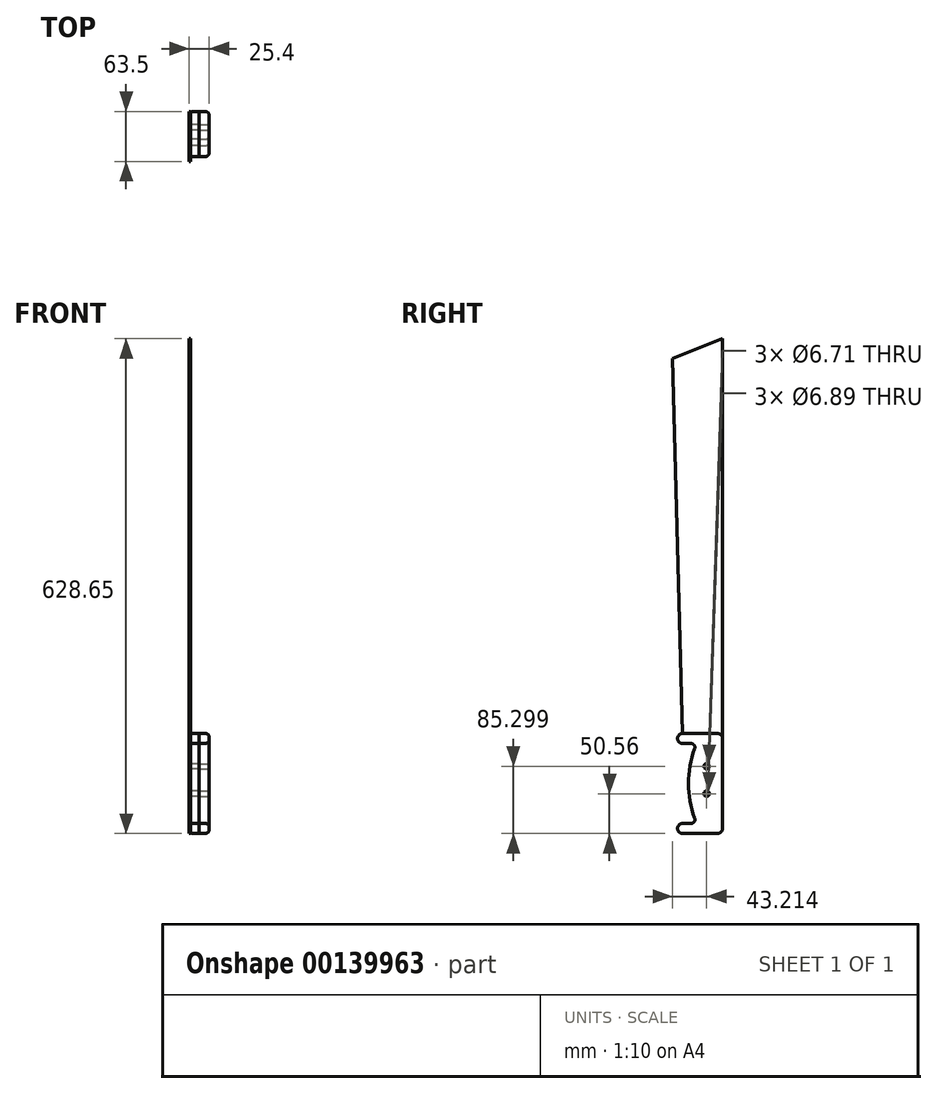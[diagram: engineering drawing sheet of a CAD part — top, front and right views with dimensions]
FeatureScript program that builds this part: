
annotation { "Feature Type Name" : "Feature", "Feature Type Description" : "" }
export const myFeature = defineFeature(function(context is Context, id is Id, definition is map)
    precondition{}
    {
        {
            var Q0;
            Q0=qCreatedBy(makeId("Right.planeOp"),FACE);
            var sketch = newSketch(context, id + "F0", { "sketchPlane" : qUnion([Q0])});
            skLineSegment(sketch, "E0", {"start": v(23.33, 47.25) * mm, "end": v(23.33, -67.05) * mm});
            skLineSegment(sketch, "E1", {"start": v(16.98, -73.4) * mm, "end": v(-27.47, -73.4) * mm});
            skLineSegment(sketch, "E2", {"start": v(-33.82, -67.05) * mm, "end": v(-33.82, -67.05) * mm});
            skLineSegment(sketch, "E3", {"start": v(-27.47, -60.7) * mm, "end": v(-9.42, -60.7) * mm});
            skLineSegment(sketch, "E4", {"start": v(-9.42, -60.7) * mm, "end": v(-9.42, 40.9) * mm});
            skLineSegment(sketch, "E5", {"start": v(-9.42, 40.9) * mm, "end": v(-27.47, 40.9) * mm});
            skLineSegment(sketch, "E6", {"start": v(-33.82, 47.25) * mm, "end": v(-33.82, 47.25) * mm});
            skLineSegment(sketch, "E7", {"start": v(-27.47, 53.6) * mm, "end": v(16.98, 53.6) * mm});
            skCircle(sketch, "E8", {"center": v(3.04, 11.9) * mm, "radius": 3.36 * mm});
            skCircle(sketch, "E9", {"center": v(3.04, -22.84) * mm, "radius": 3.44 * mm});
            skPoint(sketch, "E10.visualSharp", {"position": v(-33.82, 53.6) * mm});
            skArc(sketch, "E10.filletArc", {"start": v(-27.47, 53.6) * mm, "mid": v(-31.96, 51.74) * mm, "end": v(-33.82, 47.25) * mm});
            skPoint(sketch, "E11.visualSharp", {"position": v(-33.82, 40.9) * mm});
            skArc(sketch, "E11.filletArc", {"start": v(-33.82, 47.25) * mm, "mid": v(-31.96, 42.75) * mm, "end": v(-27.47, 40.9) * mm});
            skPoint(sketch, "E12.visualSharp", {"position": v(23.33, 53.6) * mm});
            skArc(sketch, "E12.filletArc", {"start": v(23.33, 47.25) * mm, "mid": v(21.47, 51.74) * mm, "end": v(16.98, 53.6) * mm});
            skPoint(sketch, "E13.visualSharp", {"position": v(23.33, -73.4) * mm});
            skArc(sketch, "E13.filletArc", {"start": v(16.98, -73.4) * mm, "mid": v(21.47, -71.55) * mm, "end": v(23.33, -67.05) * mm});
            skPoint(sketch, "E14.visualSharp", {"position": v(-33.82, -73.4) * mm});
            skArc(sketch, "E14.filletArc", {"start": v(-33.82, -67.05) * mm, "mid": v(-31.96, -71.55) * mm, "end": v(-27.47, -73.4) * mm});
            skPoint(sketch, "E15.visualSharp", {"position": v(-33.82, -60.7) * mm});
            skArc(sketch, "E15.filletArc", {"start": v(-27.47, -60.7) * mm, "mid": v(-31.96, -62.56) * mm, "end": v(-33.82, -67.05) * mm});
            skPoint(sketch, "E16.visualSharp", {"position": v(-9.42, -60.7) * mm});
            skLineSegment(sketch, "E16.filletArc", {"start": v(-9.42, -60.7) * mm, "end": v(-9.42, -60.7) * mm});
            skPoint(sketch, "E17.visualSharp", {"position": v(-9.42, 40.9) * mm});
            skLineSegment(sketch, "E17.filletArc", {"start": v(-9.42, 40.9) * mm, "end": v(-9.42, 40.9) * mm});
            skArc(sketch, "E18", {"start": v(-9.42, 40.9) * mm, "mid": v(-20, -9.9) * mm, "end": v(-9.42, -60.7) * mm});
            skSolve(sketch);
        }
        {
            var Q0;
            Q0 = qSketchRegion(id + "F0", true);
            extrude(context, id + "F1", {"entities" : qUnion([Q0]), "depth" : 12.7 * mm, "offsetDistance" : 25.4 * mm});
        }
        {
            var Q0;
            Q0=makeQuery(id+"F1.opExtrude","CAP_EDGE",EDGE,{"disambiguationData":[OSD([sQuery(id+"F0.wireOp",EDGE,"E7")])],"isStart":true});
            var Q1;
            Q1=makeQuery(id+"F1.opExtrude","CAP_EDGE",EDGE,{"disambiguationData":[OSD([sQuery(id+"F0.wireOp",EDGE,"E18")])],"isStart":true});
            var Q2;
            Q2=makeQuery(id+"F1.opExtrude","SWEPT_EDGE",EDGE,{"disambiguationData":[OSD([sQuery(id+"F0.wireOp",EDGE,"E4"),sQuery(id+"F0.wireOp",EDGE,"E5"),sQuery(id+"F0.wireOp",EDGE,"E18")])]});
            var Q3;
            Q3=makeQuery(id+"F1.opExtrude","SWEPT_EDGE",EDGE,{"disambiguationData":[OSD([sQuery(id+"F0.wireOp",EDGE,"E3"),sQuery(id+"F0.wireOp",EDGE,"E4"),sQuery(id+"F0.wireOp",EDGE,"E18")])]});
            fillet(context, id + "F2", {"entities" : qUnion([Q0, Q1, Q2, Q3]), "radius" : 5.08 * mm, "tangentPropagation" : true, "allowEdgeOverflow" : false});
        }
        {
            var Q0;
            Q0=makeQuery(id+"F1.opExtrude","SWEPT_BODY",BODY,{"disambiguationData":[OSD([sQuery(id+"F0.wireOp",EDGE,"E0"),sQuery(id+"F0.wireOp",EDGE,"E1"),sQuery(id+"F0.wireOp",EDGE,"E3"),sQuery(id+"F0.wireOp",EDGE,"E4"),sQuery(id+"F0.wireOp",EDGE,"E5"),sQuery(id+"F0.wireOp",EDGE,"E7"),sQuery(id+"F0.wireOp",EDGE,"E8"),sQuery(id+"F0.wireOp",EDGE,"E9"),sQuery(id+"F0.wireOp",EDGE,"E10.filletArc"),sQuery(id+"F0.wireOp",EDGE,"E11.filletArc"),sQuery(id+"F0.wireOp",EDGE,"E12.filletArc"),sQuery(id+"F0.wireOp",EDGE,"E13.filletArc"),sQuery(id+"F0.wireOp",EDGE,"E14.filletArc"),sQuery(id+"F0.wireOp",EDGE,"E15.filletArc")])]});
            var Q1;
            Q1=makeQuery(id+"F1.opExtrude","CAP_FACE",FACE,{"disambiguationData":[OSD([sQuery(id+"F0.wireOp",EDGE,"E0"),sQuery(id+"F0.wireOp",EDGE,"E1"),sQuery(id+"F0.wireOp",EDGE,"E3"),sQuery(id+"F0.wireOp",EDGE,"E4"),sQuery(id+"F0.wireOp",EDGE,"E5"),sQuery(id+"F0.wireOp",EDGE,"E7"),sQuery(id+"F0.wireOp",EDGE,"E8"),sQuery(id+"F0.wireOp",EDGE,"E9"),sQuery(id+"F0.wireOp",EDGE,"E10.filletArc"),sQuery(id+"F0.wireOp",EDGE,"E11.filletArc"),sQuery(id+"F0.wireOp",EDGE,"E12.filletArc"),sQuery(id+"F0.wireOp",EDGE,"E13.filletArc"),sQuery(id+"F0.wireOp",EDGE,"E14.filletArc"),sQuery(id+"F0.wireOp",EDGE,"E15.filletArc")])],"isStart":false});
            mirror(context, id + "F3", {"entities" : qUnion([Q0]), "mirrorPlane" : qUnion([Q1])});
        }
        {
            var Q0;
            Q0=qCreatedBy(makeId("Right.planeOp"),FACE);
            var sketch = newSketch(context, id + "F4", { "sketchPlane" : qUnion([Q0])});
            skLineSegment(sketch, "E19.0", {"start": v(-27.47, 40.9) * mm, "end": v(-16.93, 40.9) * mm});
            skArc(sketch, "E19.1", {"start": v(-27.47, 53.6) * mm, "mid": v(-33.82, 47.25) * mm, "end": v(-27.47, 40.9) * mm});
            skLineSegment(sketch, "E19.4", {"start": v(23.33, -67.05) * mm, "end": v(23.33, 47.25) * mm});
            skArc(sketch, "E19.5", {"start": v(16.98, -73.4) * mm, "mid": v(21.47, -71.55) * mm, "end": v(23.33, -67.05) * mm});
            skLineSegment(sketch, "E19.6", {"start": v(-27.47, -73.4) * mm, "end": v(16.98, -73.4) * mm});
            skArc(sketch, "E19.7", {"start": v(-27.47, -60.7) * mm, "mid": v(-33.82, -67.05) * mm, "end": v(-27.47, -73.4) * mm});
            skLineSegment(sketch, "E19.8", {"start": v(-16.93, -60.7) * mm, "end": v(-27.47, -60.7) * mm});
            skArc(sketch, "E19.9", {"start": v(-16.93, -60.7) * mm, "mid": v(-12.76, -58.53) * mm, "end": v(-12.16, -53.87) * mm});
            skArc(sketch, "E19.10", {"start": v(-12.16, 34.06) * mm, "mid": v(-20, -9.9) * mm, "end": v(-12.16, -53.87) * mm});
            skArc(sketch, "E19.11", {"start": v(-12.16, 34.06) * mm, "mid": v(-12.76, 38.72) * mm, "end": v(-16.93, 40.9) * mm});
            skCircle(sketch, "E19.12", {"center": v(3.04, 11.9) * mm, "radius": 3.36 * mm});
            skCircle(sketch, "E19.13", {"center": v(3.04, -22.84) * mm, "radius": 3.44 * mm});
            skLineSegment(sketch, "E20", {"start": v(23.33, 47.25) * mm, "end": v(23.33, 555.25) * mm});
            skLineSegment(sketch, "E21", {"start": v(23.33, 555.25) * mm, "end": v(-40.17, 529.85) * mm});
            skLineSegment(sketch, "E22", {"start": v(-40.17, 529.85) * mm, "end": v(-27.47, 53.6) * mm});
            skSolve(sketch);
        }
        {
            var Q0;
            Q0 = qSketchRegion(id + "F4", true);
            extrude(context, id + "F5", {"entities" : qUnion([Q0]), "depth" : 1.9 * mm, "offsetDistance" : 25.4 * mm});
        }
    });
